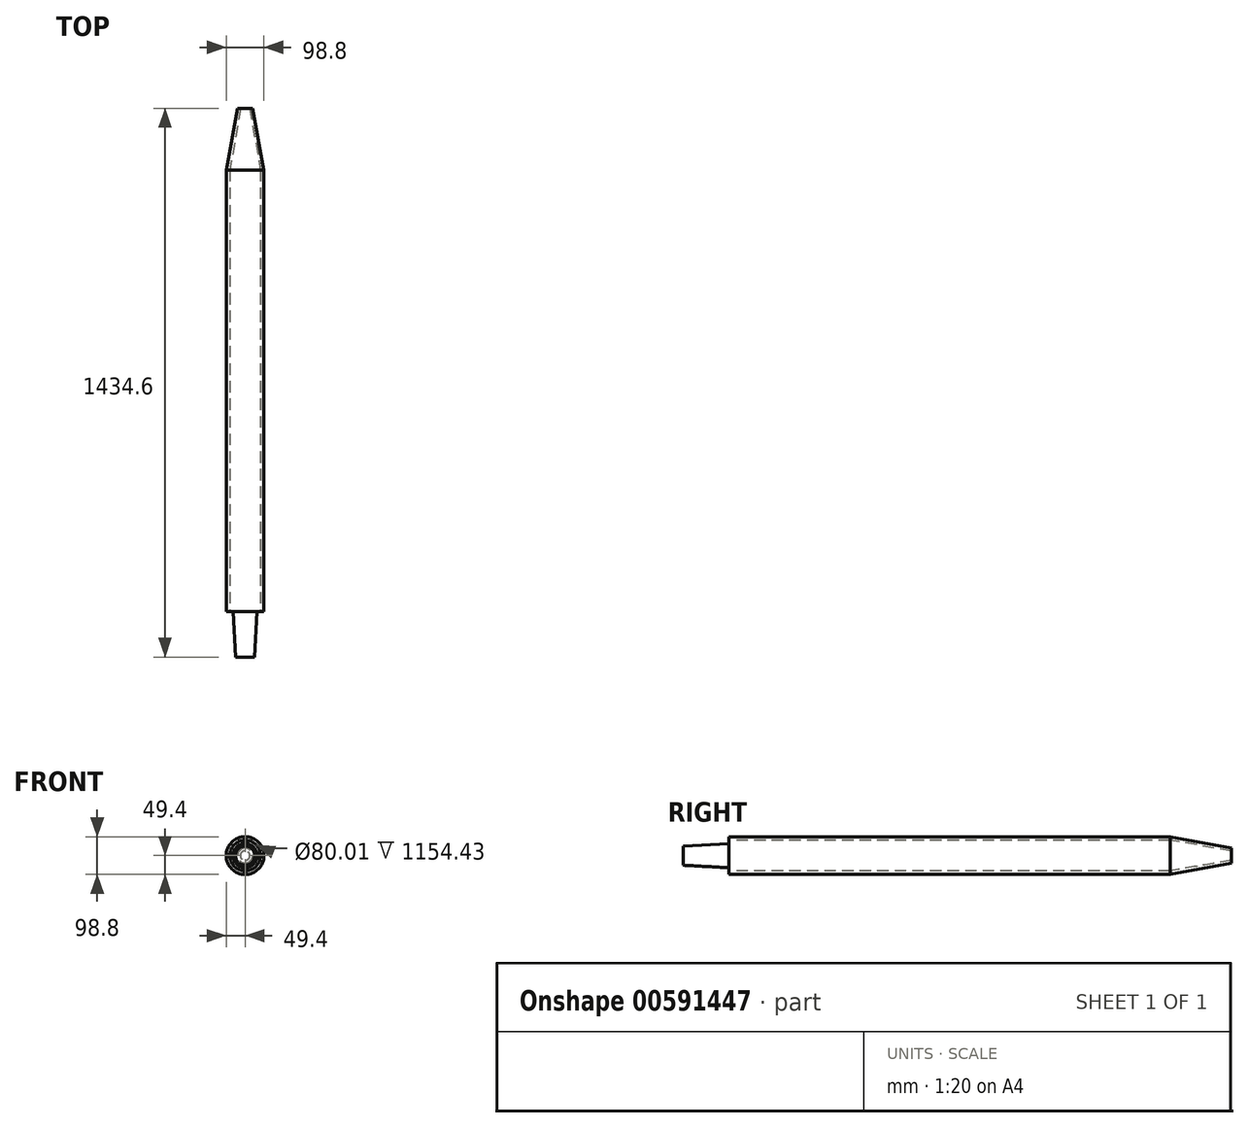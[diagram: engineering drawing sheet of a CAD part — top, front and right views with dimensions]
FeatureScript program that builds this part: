
annotation { "Feature Type Name" : "Feature", "Feature Type Description" : "" }
export const myFeature = defineFeature(function(context is Context, id is Id, definition is map)
    precondition{}
    {
        {
            var Q0;
            Q0=qCreatedBy(makeId("Front.planeOp"),FACE);
            var sketch = newSketch(context, id + "F0", { "sketchPlane" : qUnion([Q0])});
            skCircle(sketch, "E0", {"center": v(0, 0) * mm, "radius": 49.4 * mm});
            skSolve(sketch);
        }
        {
            var Q0;
            Q0=makeQuery(id+"F0.imprint","IMPRINT",FACE,{"disambiguationData":[TD([[makeQuery(id+"F0.imprint","IMPRINT",EDGE,{"derivedFrom":sQuery(id+"F0.wireOp",EDGE,"E0")}),1.0]])]});
            var Q1;
            Q1=sQuery(id+"F0.wireOp",EDGE,"E0");
            extrude(context, id + "F1", {"entities" : qUnion([Q0]), "surfaceEntities" : qUnion([Q1]), "endBound" : BoundingType.SYMMETRIC, "depth" : 1154.43 * mm, "offsetDistance" : 25.4 * mm});
        }
        {
            var Q0;
            Q0=makeQuery(id+"F1.opExtrude","CAP_FACE",FACE,{"disambiguationData":[OSD([sQuery(id+"F0.wireOp",EDGE,"E0")])],"isStart":false});
            var sketch = newSketch(context, id + "F2", { "sketchPlane" : qUnion([Q0])});
            skCircle(sketch, "E1", {"center": v(0, 0) * mm, "radius": 40 * mm});
            skSolve(sketch);
        }
        {
            var Q0;
            Q0=makeQuery(id+"F2.imprint","IMPRINT",FACE,{"disambiguationData":[TD([[makeQuery(id+"F2.imprint","IMPRINT",EDGE,{"derivedFrom":sQuery(id+"F2.wireOp",EDGE,"E1")}),1.0]])]});
            extrude(context, id + "F3", {"entities" : qUnion([Q0]), "operationType" : NewBodyOperationType.REMOVE, "endBound" : BoundingType.THROUGH_ALL, "oppositeDirection" : true, "depth" : 25.4 * mm, "offsetDistance" : 25.4 * mm});
        }
        {
            var Q0;
            Q0=makeQuery(id+"F1.opExtrude","CAP_FACE",FACE,{"disambiguationData":[OSD([sQuery(id+"F0.wireOp",EDGE,"E0")])],"isStart":false});
            var sketch = newSketch(context, id + "F4", { "sketchPlane" : qUnion([Q0])});
            skCircle(sketch, "E2", {"center": v(0, 0) * mm, "radius": 31.62 * mm});
            skSolve(sketch);
        }
        {
            var Q0;
            Q0=makeQuery(id+"F4.imprint","IMPRINT",FACE,{"disambiguationData":[TD([[makeQuery(id+"F4.imprint","IMPRINT",EDGE,{"derivedFrom":sQuery(id+"F4.wireOp",EDGE,"E2")}),1.0]])]});
            cPlane(context, id + "F5", {"entities" : qUnion([Q0]), "cplaneType" : CPlaneType.OFFSET, "offset" : 119.38 * mm, "width" : 152.4 * mm, "height" : 152.4 * mm});
        }
        {
            var Q0;
            Q0=qCreatedBy(id+"F5.planeOp",FACE);
            var sketch = newSketch(context, id + "F6", { "sketchPlane" : qUnion([Q0])});
            skCircle(sketch, "E3", {"center": v(0, 0) * mm, "radius": 25.15 * mm});
            skSolve(sketch);
        }
        {
            var Q0;
            Q0=makeQuery(id+"F4.imprint","IMPRINT",FACE,{"disambiguationData":[TD([[makeQuery(id+"F4.imprint","IMPRINT",EDGE,{"derivedFrom":sQuery(id+"F4.wireOp",EDGE,"E2")}),1.0]])]});
            var Q1;
            Q1=makeQuery(id+"F6.imprint","IMPRINT",FACE,{"disambiguationData":[TD([[makeQuery(id+"F6.imprint","IMPRINT",EDGE,{"derivedFrom":sQuery(id+"F6.wireOp",EDGE,"E3")}),1.0]])]});
            loft(context, id + "F7", {"sheetProfilesArray" : [{ "sheetProfileEntities" : qUnion([Q0]) }, { "sheetProfileEntities" : qUnion([Q1]) }]});
        }
        {
            var Q0;
            Q0=makeQuery(id+"F1.opExtrude","CAP_FACE",FACE,{"disambiguationData":[OSD([sQuery(id+"F0.wireOp",EDGE,"E0")])],"isStart":true});
            cPlane(context, id + "F8", {"entities" : qUnion([Q0]), "cplaneType" : CPlaneType.OFFSET, "offset" : 160.78 * mm, "width" : 152.4 * mm, "height" : 152.4 * mm});
        }
        {
            var Q0;
            Q0=qCreatedBy(id+"F8.planeOp",FACE);
            var sketch = newSketch(context, id + "F9", { "sketchPlane" : qUnion([Q0])});
            skCircle(sketch, "E4", {"center": v(0, 0) * mm, "radius": 19.43 * mm});
            skSolve(sketch);
        }
        {
            var Q0;
            Q0=makeQuery(id+"F1.opExtrude","CAP_FACE",FACE,{"disambiguationData":[OSD([sQuery(id+"F0.wireOp",EDGE,"E0")])],"isStart":true});
            var sketch = newSketch(context, id + "F10", { "sketchPlane" : qUnion([Q0])});
            skCircle(sketch, "E5", {"center": v(0, 0) * mm, "radius": 49.4 * mm});
            skSolve(sketch);
        }
        {
            var Q1;
            Q1 = qSketchRegion(id + "F9", true);
            var Q2;
            Q2 = qSketchRegion(id + "F10", true);
            loft(context, id + "F11", {"sheetProfilesArray" : [{ "sheetProfileEntities" : qUnion([Q1]) }, { "sheetProfileEntities" : qUnion([Q2]) }]});
        }
        {
            var Q0;
            Q0=makeQuery(id+"F11.opLoft","CAP_FACE",FACE,{"disambiguationData":[OSD([makeQuery(id+"F9.imprint","IMPRINT",FACE,{"disambiguationData":[TD([[makeQuery(id+"F9.imprint","IMPRINT",EDGE,{"derivedFrom":sQuery(id+"F9.wireOp",EDGE,"E4")}),1.0]])]})])],"isStart":true});
            var sketch = newSketch(context, id + "F12", { "sketchPlane" : qUnion([Q0])});
            skCircle(sketch, "E6", {"center": v(0, 0) * mm, "radius": 12.45 * mm});
            skSolve(sketch);
        }
        {
            var Q0;
            Q0=makeQuery(id+"F1.opExtrude","CAP_FACE",FACE,{"disambiguationData":[OSD([sQuery(id+"F0.wireOp",EDGE,"E0")])],"isStart":true});
            var sketch = newSketch(context, id + "F13", { "sketchPlane" : qUnion([Q0])});
            skCircle(sketch, "E7", {"center": v(0, 0) * mm, "radius": 40 * mm});
            skSolve(sketch);
        }
        {
            var Q1;
            Q1=makeQuery(id+"F13.imprint","IMPRINT",FACE,{"disambiguationData":[TD([[makeQuery(id+"F13.imprint","IMPRINT",EDGE,{"derivedFrom":sQuery(id+"F13.wireOp",EDGE,"E7")}),-1.0]])]});
            var Q2;
            Q2=makeQuery(id+"F12.imprint","IMPRINT",FACE,{"disambiguationData":[TD([[makeQuery(id+"F12.imprint","IMPRINT",EDGE,{"derivedFrom":sQuery(id+"F12.wireOp",EDGE,"E6")}),1.0]])]});
            loft(context, id + "F14", {"operationType" : NewBodyOperationType.REMOVE, "sheetProfilesArray" : [{ "sheetProfileEntities" : qUnion([Q1]) }, { "sheetProfileEntities" : qUnion([Q2]) }]});
        }
    });
